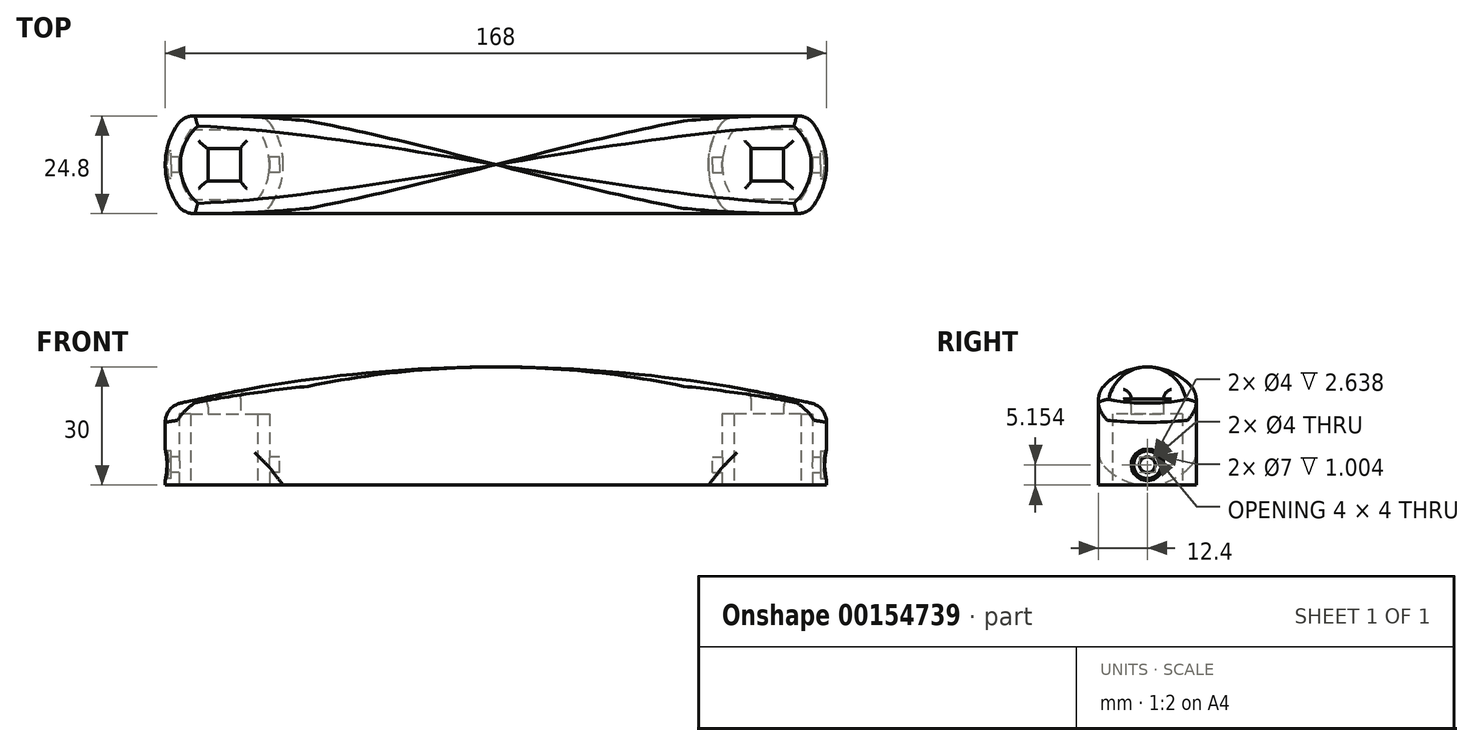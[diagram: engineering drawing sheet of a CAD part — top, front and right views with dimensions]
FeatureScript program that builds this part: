
annotation { "Feature Type Name" : "Feature", "Feature Type Description" : "" }
export const myFeature = defineFeature(function(context is Context, id is Id, definition is map)
    precondition{}
    {
        {
            var Q0;
            Q0=qCreatedBy(makeId("Top.planeOp"),FACE);
            var sketch = newSketch(context, id + "F0", { "sketchPlane" : qUnion([Q0])});
            skLineSegment(sketch, "E0.bottom", {"start": v(-80.5, 8.9) * mm, "end": v(-77.5, 8.9) * mm, "construction": true});
            skLineSegment(sketch, "E0.top", {"start": v(-80.5, -8.9) * mm, "end": v(-77.5, -8.9) * mm, "construction": true});
            skLineSegment(sketch, "E0.left", {"start": v(-80.5, 8.9) * mm, "end": v(-80.5, -8.9) * mm, "construction": true});
            skLineSegment(sketch, "E0.right", {"start": v(-57.5, 8.9) * mm, "end": v(-57.5, -8.9) * mm, "construction": true});
            skArc(sketch, "E1", {"start": v(-77.5, 8.9) * mm, "mid": v(-80.5, 0) * mm, "end": v(-77.5, -8.9) * mm});
            skLineSegment(sketch, "E2", {"start": v(-69, 8.9) * mm, "end": v(-69, -8.9) * mm, "construction": true});
            skArc(sketch, "E3.MirrorCS", {"start": v(-60.5, 8.9) * mm, "mid": v(-57.5, 0) * mm, "end": v(-60.5, -8.9) * mm});
            skLineSegment(sketch, "E4", {"start": v(-80.5, 0) * mm, "end": v(-57.5, 0) * mm, "construction": true});
            skPoint(sketch, "E4.startSnap0", {"position": v(-80.5, 0) * mm});
            skLineSegment(sketch, "E5", {"start": v(-77.5, 8.9) * mm, "end": v(-77.5, -8.9) * mm, "construction": true});
            skLineSegment(sketch, "E6", {"start": v(0, 8.37) * mm, "end": v(0, -11.71) * mm, "construction": true});
            skLineSegment(sketch, "E7", {"start": v(-77.5, 8.9) * mm, "end": v(-60.5, 8.9) * mm});
            skLineSegment(sketch, "E8", {"start": v(-60.5, 8.9) * mm, "end": v(-57.5, 8.9) * mm, "construction": true});
            skLineSegment(sketch, "E9", {"start": v(-60.5, -8.9) * mm, "end": v(-60.5, -8.9) * mm});
            skLineSegment(sketch, "E10", {"start": v(-77.5, -8.9) * mm, "end": v(-60.5, -8.9) * mm});
            skLineSegment(sketch, "E11", {"start": v(-60.5, -8.9) * mm, "end": v(-57.5, -8.9) * mm, "construction": true});
            skSolve(sketch);
        }
        {
            var Q0;
            Q0=qCreatedBy(makeId("Top.planeOp"),FACE);
            var sketch = newSketch(context, id + "F1", { "sketchPlane" : qUnion([Q0])});
            skLineSegment(sketch, "E12.0", {"start": v(-79.12, 12.4) * mm, "end": v(-58.88, 12.4) * mm});
            skArc(sketch, "E12.1", {"start": v(-79.12, 12.4) * mm, "mid": v(-84, 0) * mm, "end": v(-79.12, -12.4) * mm});
            skLineSegment(sketch, "E12.2", {"start": v(-79.12, -12.4) * mm, "end": v(-58.88, -12.4) * mm});
            skArc(sketch, "E12.3", {"start": v(-58.88, 12.4) * mm, "mid": v(-54, 0) * mm, "end": v(-58.88, -12.4) * mm});
            skLineSegment(sketch, "E13", {"start": v(-84, 0) * mm, "end": v(-84, 12.4) * mm, "construction": true});
            skSolve(sketch);
        }
        {
            var Q0;
            Q0=qCreatedBy(makeId("Front.planeOp"),FACE);
            var sketch = newSketch(context, id + "F2", { "sketchPlane" : qUnion([Q0])});
            skLineSegment(sketch, "E14", {"start": v(0, 15) * mm, "end": v(-39.65, 15) * mm, "construction": true});
            skPoint(sketch, "E15.oppositeSnap0", {"position": v(-19.82, 15) * mm});
            skLineSegment(sketch, "E15.bottom", {"start": v(0, 0) * mm, "end": v(-95, 0) * mm});
            skLineSegment(sketch, "E15.top", {"start": v(0, 15) * mm, "end": v(-95, 15) * mm});
            skLineSegment(sketch, "E15.left", {"start": v(0, 0) * mm, "end": v(0, 15) * mm});
            skLineSegment(sketch, "E15.right", {"start": v(-95, 0) * mm, "end": v(-95, 15) * mm});
            skSolve(sketch);
        }
        {
            var Q0;
            Q0=qSketchRegion(id+"F2",true);
            var Q1;
            Q1=sQuery(id+"F2.wireOp",EDGE,"E15.top");
            revolve(context, id + "F3", {"entities" : qUnion([Q0]), "axis" : qUnion([Q1]), "revolveType" : RevolveType.FULL});
        }
        {
            var Q0;
            Q0=qCreatedBy(makeId("Top.planeOp"),FACE);
            var sketch = newSketch(context, id + "F4", { "sketchPlane" : qUnion([Q0])});
            skArc(sketch, "E16", {"start": v(-79.12, 12.4) * mm, "mid": v(-84, 0) * mm, "end": v(-79.12, -12.4) * mm});
            skLineSegment(sketch, "E17", {"start": v(-79.12, 12.4) * mm, "end": v(0, 12.4) * mm});
            skLineSegment(sketch, "E18", {"start": v(0, 12.4) * mm, "end": v(0, 20.08) * mm});
            skLineSegment(sketch, "E19", {"start": v(0, 20.08) * mm, "end": v(-96.67, 20.08) * mm});
            skLineSegment(sketch, "E20", {"start": v(-96.67, 20.08) * mm, "end": v(-96.67, -24.17) * mm});
            skLineSegment(sketch, "E21", {"start": v(-96.67, -24.17) * mm, "end": v(0, -24.17) * mm});
            skLineSegment(sketch, "E22", {"start": v(0, -24.17) * mm, "end": v(0, -12.4) * mm});
            skLineSegment(sketch, "E23", {"start": v(0, -12.4) * mm, "end": v(-79.12, -12.4) * mm});
            skSolve(sketch);
        }
        {
            var Q0;
            Q0=qSketchRegion(id+"F4",true);
            extrude(context, id + "F5", {"entities" : qUnion([Q0]), "operationType" : NewBodyOperationType.REMOVE, "depth" : 50 * mm});
        }
        {
            var Q0;
            Q0=qSketchRegion(id+"F1",true);
            extrude(context, id + "F6", {"entities" : qUnion([Q0]), "operationType" : NewBodyOperationType.ADD, "depth" : 23 * mm});
        }
        {
            var Q0;
            Q0=qSketchRegion(id+"F0",true);
            extrude(context, id + "F7", {"entities" : qUnion([Q0]), "operationType" : NewBodyOperationType.REMOVE, "depth" : 18 * mm});
        }
        {
            var Q0;
            Q0=makeQuery(id+"F7.boolean.opBoolean","COPY",FACE,{"derivedFrom":makeQuery(id+"F7.opExtrude","CAP_FACE",FACE,{"disambiguationData":[OSD([sQuery(id+"F0.wireOp",EDGE,"E1"),sQuery(id+"F0.wireOp",EDGE,"E3.MirrorCS"),sQuery(id+"F0.wireOp",EDGE,"E7"),sQuery(id+"F0.wireOp",EDGE,"E10")])],"isStart":false})});
            var sketch = newSketch(context, id + "F8", { "sketchPlane" : qUnion([Q0])});
            skLineSegment(sketch, "E24.bottom", {"start": v(-73.13, 4.12) * mm, "end": v(-64.87, 4.12) * mm});
            skLineSegment(sketch, "E24.top", {"start": v(-73.13, -4.12) * mm, "end": v(-64.87, -4.12) * mm});
            skLineSegment(sketch, "E24.left", {"start": v(-73.13, 4.12) * mm, "end": v(-73.13, -4.12) * mm});
            skLineSegment(sketch, "E24.right", {"start": v(-64.88, 4.13) * mm, "end": v(-64.88, -4.13) * mm});
            skLineSegment(sketch, "E25", {"start": v(-69, 4.12) * mm, "end": v(-69, -4.12) * mm, "construction": true});
            skLineSegment(sketch, "E26", {"start": v(-73.13, 0) * mm, "end": v(-64.88, 0) * mm, "construction": true});
            skSolve(sketch);
        }
        {
            var Q0;
            Q0=qSketchRegion(id+"F8",true);
            var Q1;
            Q1=makeQuery(id+"F6.opExtrude","CAP_FACE",FACE,{"disambiguationData":[OSD([sQuery(id+"F1.wireOp",EDGE,"E12.0"),sQuery(id+"F1.wireOp",EDGE,"E12.1"),sQuery(id+"F1.wireOp",EDGE,"E12.2"),sQuery(id+"F1.wireOp",EDGE,"E12.3")])],"isStart":false});
            extrude(context, id + "F9", {"entities" : qUnion([Q0]), "operationType" : NewBodyOperationType.REMOVE, "endBound" : BoundingType.THROUGH_ALL, "oppositeDirection" : true, "endBoundEntityFace" : qUnion([Q1]), "depth" : 25 * mm});
        }
        {
            var Q0;
            Q0=qCreatedBy(makeId("Right.planeOp"),FACE);
            cPlane(context, id + "F10", {"entities" : qUnion([Q0]), "cplaneType" : CPlaneType.OFFSET, "offset" : 90 * mm, "oppositeDirection" : true, "width" : 150 * mm, "height" : 150 * mm});
        }
        {
            var Q0;
            Q0=qCreatedBy(id+"F10.planeOp",FACE);
            var sketch = newSketch(context, id + "F11", { "sketchPlane" : qUnion([Q0])});
            skCircle(sketch, "E27", {"center": v(0, 5.15) * mm, "radius": 2 * mm});
            skSolve(sketch);
        }
        {
            var Q0;
            Q0=qSketchRegion(id+"F11",true);
            extrude(context, id + "F12", {"entities" : qUnion([Q0]), "operationType" : NewBodyOperationType.REMOVE, "depth" : 35 * mm});
        }
        {
            var Q0;
            Q0=qCreatedBy(id+"F10.planeOp",FACE);
            var sketch = newSketch(context, id + "F13", { "sketchPlane" : qUnion([Q0])});
            skCircle(sketch, "E28", {"center": v(0, 5.15) * mm, "radius": 3.5 * mm});
            skSolve(sketch);
        }
        {
            var Q0;
            Q0=qSketchRegion(id+"F13",true);
            extrude(context, id + "F14", {"entities" : qUnion([Q0]), "operationType" : NewBodyOperationType.REMOVE, "depth" : 7.5 * mm});
        }
        {
            var Q0;
            Q0=qCreatedBy(makeId("Front.planeOp"),FACE);
            var sketch = newSketch(context, id + "F15", { "sketchPlane" : qUnion([Q0])});
            skLineSegment(sketch, "E29", {"start": v(-64.87, 24) * mm, "end": v(-80.29, 24) * mm, "construction": true});
            skLineSegment(sketch, "E30", {"start": v(-64.87, 18) * mm, "end": v(-80.42, 18) * mm, "construction": true});
            skLineSegment(sketch, "E31", {"start": v(-64.87, 24) * mm, "end": v(-64.87, 18) * mm, "construction": true});
            skSolve(sketch);
        }
        {
            var Q0;
            Q0=qCreatedBy(makeId("Front.planeOp"),FACE);
            var sketch = newSketch(context, id + "F16", { "sketchPlane" : qUnion([Q0])});
            skArc(sketch, "E32", {"start": v(-133.08, 4.01) * mm, "mid": v(-67.8, 23.44) * mm, "end": v(0, 30) * mm});
            skLineSegment(sketch, "E33", {"start": v(0, 30) * mm, "end": v(-86, 30) * mm, "construction": true});
            skLineSegment(sketch, "E34", {"start": v(-86, 30) * mm, "end": v(-86, 0) * mm, "construction": true});
            skLineSegment(sketch, "E35", {"start": v(-133.08, 4.01) * mm, "end": v(-142.12, 0.34) * mm});
            skLineSegment(sketch, "E36", {"start": v(-142.12, 0.34) * mm, "end": v(-142.12, 44.58) * mm});
            skLineSegment(sketch, "E37", {"start": v(-142.12, 44.58) * mm, "end": v(0, 44.58) * mm});
            skLineSegment(sketch, "E38", {"start": v(0, 44.58) * mm, "end": v(0, 30) * mm});
            skPoint(sketch, "E39", {"position": v(-86, 15) * mm});
            skPoint(sketch, "E40", {"position": v(-64.47, 21.36) * mm});
            skPoint(sketch, "E41", {"position": v(-100.39, 15.46) * mm});
            skSolve(sketch);
        }
        {
            var Q0;
            Q0=qSketchRegion(id+"F16",true);
            extrude(context, id + "F17", {"entities" : qUnion([Q0]), "operationType" : NewBodyOperationType.REMOVE, "oppositeDirection" : true, "depth" : 50 * mm, "symmetric" : true});
        }
        {
            var Q0;
            Q0=makeQuery(id+"F5.boolean.opBoolean","INTERSECT",EDGE,{"disambiguationData":[OD(1.0)],"derivedFrom":[makeQuery(id+"F3.opRevolve","SWEPT_FACE",FACE,{"disambiguationData":[OSD([sQuery(id+"F2.wireOp",EDGE,"E15.bottom")])]}),makeQuery(id+"F5.opExtrude","SWEPT_FACE",FACE,{"disambiguationData":[OSD([sQuery(id+"F4.wireOp",EDGE,"E17")])]})]});
            var Q1;
            Q1=makeQuery(id+"F17.boolean.opBoolean","INTERSECT",EDGE,{"disambiguationData":[OD(0.0)],"derivedFrom":[makeQuery(id+"F5.boolean.opBoolean","SPLIT",FACE,{"disambiguationData":[OD(1.0)],"derivedFrom":makeQuery(id+"F3.opRevolve","SWEPT_FACE",FACE,{"disambiguationData":[OSD([sQuery(id+"F2.wireOp",EDGE,"E15.bottom")])]})}),makeQuery(id+"F17.opExtrude","SWEPT_FACE",FACE,{"disambiguationData":[OSD([sQuery(id+"F16.wireOp",EDGE,"E32")])]})]});
            var Q2;
            Q2=makeQuery(id+"F6.boolean.opBoolean","MERGE",EDGE,{"derivedFrom":[makeQuery(id+"F5.boolean.opBoolean","COPY",EDGE,{"derivedFrom":makeQuery(id+"F5.opExtrude","SWEPT_EDGE",EDGE,{"disambiguationData":[OSD([sQuery(id+"F4.wireOp",EDGE,"E16"),sQuery(id+"F4.wireOp",EDGE,"E17")])]})}),makeQuery(id+"F6.opExtrude","SWEPT_EDGE",EDGE,{"disambiguationData":[OSD([sQuery(id+"F1.wireOp",EDGE,"E12.0"),sQuery(id+"F1.wireOp",EDGE,"E12.1")])]})]});
            var Q3;
            Q3=makeQuery(id+"F17.boolean.opBoolean","INTERSECT",EDGE,{"derivedFrom":[makeQuery(id+"F6.boolean.opBoolean","MERGE",FACE,{"derivedFrom":[makeQuery(id+"F5.boolean.opBoolean","COPY",FACE,{"derivedFrom":makeQuery(id+"F5.opExtrude","SWEPT_FACE",FACE,{"disambiguationData":[OSD([sQuery(id+"F4.wireOp",EDGE,"E16")])]})}),makeQuery(id+"F6.opExtrude","SWEPT_FACE",FACE,{"disambiguationData":[OSD([sQuery(id+"F1.wireOp",EDGE,"E12.1")])]})]}),makeQuery(id+"F17.opExtrude","SWEPT_FACE",FACE,{"disambiguationData":[OSD([sQuery(id+"F16.wireOp",EDGE,"E32")])]})]});
            var Q4;
            Q4=makeQuery(id+"F17.boolean.opBoolean","INTERSECT",EDGE,{"disambiguationData":[OD(1.0)],"derivedFrom":[makeQuery(id+"F5.boolean.opBoolean","SPLIT",FACE,{"disambiguationData":[OD(1.0)],"derivedFrom":makeQuery(id+"F3.opRevolve","SWEPT_FACE",FACE,{"disambiguationData":[OSD([sQuery(id+"F2.wireOp",EDGE,"E15.bottom")])]})}),makeQuery(id+"F17.opExtrude","SWEPT_FACE",FACE,{"disambiguationData":[OSD([sQuery(id+"F16.wireOp",EDGE,"E32")])]})]});
            var Q5;
            Q5=makeQuery(id+"F6.opExtrude","SWEPT_EDGE",EDGE,{"disambiguationData":[OSD([sQuery(id+"F1.wireOp",EDGE,"E12.0"),sQuery(id+"F1.wireOp",EDGE,"E12.3")])]});
            var Q6;
            Q6=makeQuery(id+"F5.boolean.opBoolean","INTERSECT",EDGE,{"disambiguationData":[OD(0.0)],"derivedFrom":[makeQuery(id+"F3.opRevolve","SWEPT_FACE",FACE,{"disambiguationData":[OSD([sQuery(id+"F2.wireOp",EDGE,"E15.bottom")])]}),makeQuery(id+"F5.opExtrude","SWEPT_FACE",FACE,{"disambiguationData":[OSD([sQuery(id+"F4.wireOp",EDGE,"E17")])]})]});
            var Q7;
            Q7=makeQuery(id+"F6.boolean.opBoolean","MERGE",EDGE,{"derivedFrom":[makeQuery(id+"F5.boolean.opBoolean","COPY",EDGE,{"derivedFrom":makeQuery(id+"F5.opExtrude","SWEPT_EDGE",EDGE,{"disambiguationData":[OSD([sQuery(id+"F4.wireOp",EDGE,"E16"),sQuery(id+"F4.wireOp",EDGE,"E23")])]})}),makeQuery(id+"F6.opExtrude","SWEPT_EDGE",EDGE,{"disambiguationData":[OSD([sQuery(id+"F1.wireOp",EDGE,"E12.1"),sQuery(id+"F1.wireOp",EDGE,"E12.2")])]})]});
            var Q8;
            Q8=makeQuery(id+"F5.boolean.opBoolean","INTERSECT",EDGE,{"disambiguationData":[OD(1.0)],"derivedFrom":[makeQuery(id+"F3.opRevolve","SWEPT_FACE",FACE,{"disambiguationData":[OSD([sQuery(id+"F2.wireOp",EDGE,"E15.bottom")])]}),makeQuery(id+"F5.opExtrude","SWEPT_FACE",FACE,{"disambiguationData":[OSD([sQuery(id+"F4.wireOp",EDGE,"E23")])]})]});
            var Q9;
            Q9=makeQuery(id+"F6.opExtrude","SWEPT_EDGE",EDGE,{"disambiguationData":[OSD([sQuery(id+"F1.wireOp",EDGE,"E12.2"),sQuery(id+"F1.wireOp",EDGE,"E12.3")])]});
            var Q10;
            Q10=makeQuery(id+"F5.boolean.opBoolean","INTERSECT",EDGE,{"disambiguationData":[OD(0.0)],"derivedFrom":[makeQuery(id+"F3.opRevolve","SWEPT_FACE",FACE,{"disambiguationData":[OSD([sQuery(id+"F2.wireOp",EDGE,"E15.bottom")])]}),makeQuery(id+"F5.opExtrude","SWEPT_FACE",FACE,{"disambiguationData":[OSD([sQuery(id+"F4.wireOp",EDGE,"E23")])]})]});
            fillet(context, id + "F18", {"entities" : qUnion([Q0, Q1, Q2, Q3, Q4, Q5, Q6, Q7, Q8, Q9, Q10]), "radius" : 5 * mm, "tangentPropagation" : true, "allowEdgeOverflow" : false});
        }
        {
            var Q0;
            Q0=makeQuery(id+"F17.boolean.opBoolean","INTERSECT",EDGE,{"derivedFrom":[makeQuery(id+"F9.boolean.opBoolean","COPY",FACE,{"derivedFrom":makeQuery(id+"F9.opExtrude","SWEPT_FACE",FACE,{"disambiguationData":[OSD([sQuery(id+"F8.wireOp",EDGE,"E24.top")])]})}),makeQuery(id+"F17.opExtrude","SWEPT_FACE",FACE,{"disambiguationData":[OSD([sQuery(id+"F16.wireOp",EDGE,"E32")])]})]});
            var Q1;
            Q1=makeQuery(id+"F17.boolean.opBoolean","INTERSECT",EDGE,{"derivedFrom":[makeQuery(id+"F9.boolean.opBoolean","COPY",FACE,{"derivedFrom":makeQuery(id+"F9.opExtrude","SWEPT_FACE",FACE,{"disambiguationData":[OSD([sQuery(id+"F8.wireOp",EDGE,"E24.right")])]})}),makeQuery(id+"F17.opExtrude","SWEPT_FACE",FACE,{"disambiguationData":[OSD([sQuery(id+"F16.wireOp",EDGE,"E32")])]})]});
            var Q2;
            Q2=makeQuery(id+"F17.boolean.opBoolean","INTERSECT",EDGE,{"derivedFrom":[makeQuery(id+"F9.boolean.opBoolean","COPY",FACE,{"derivedFrom":makeQuery(id+"F9.opExtrude","SWEPT_FACE",FACE,{"disambiguationData":[OSD([sQuery(id+"F8.wireOp",EDGE,"E24.left")])]})}),makeQuery(id+"F17.opExtrude","SWEPT_FACE",FACE,{"disambiguationData":[OSD([sQuery(id+"F16.wireOp",EDGE,"E32")])]})]});
            var Q3;
            Q3=makeQuery(id+"F17.boolean.opBoolean","INTERSECT",EDGE,{"derivedFrom":[makeQuery(id+"F9.boolean.opBoolean","COPY",FACE,{"derivedFrom":makeQuery(id+"F9.opExtrude","SWEPT_FACE",FACE,{"disambiguationData":[OSD([sQuery(id+"F8.wireOp",EDGE,"E24.bottom")])]})}),makeQuery(id+"F17.opExtrude","SWEPT_FACE",FACE,{"disambiguationData":[OSD([sQuery(id+"F16.wireOp",EDGE,"E32")])]})]});
            fillet(context, id + "F19", {"entities" : qUnion([Q0, Q1, Q2, Q3]), "radius" : 2 * mm, "tangentPropagation" : true, "allowEdgeOverflow" : false});
        }
        {
            var Q0;
            Q0=makeQuery(id+"F14.boolean.opBoolean","INTERSECT",EDGE,{"derivedFrom":[makeQuery(id+"F6.boolean.opBoolean","MERGE",FACE,{"derivedFrom":[makeQuery(id+"F5.boolean.opBoolean","COPY",FACE,{"derivedFrom":makeQuery(id+"F5.opExtrude","SWEPT_FACE",FACE,{"disambiguationData":[OSD([sQuery(id+"F4.wireOp",EDGE,"E16")])]})}),makeQuery(id+"F6.opExtrude","SWEPT_FACE",FACE,{"disambiguationData":[OSD([sQuery(id+"F1.wireOp",EDGE,"E12.1")])]})]}),makeQuery(id+"F14.opExtrude","SWEPT_FACE",FACE,{"disambiguationData":[OSD([sQuery(id+"F13.wireOp",EDGE,"E28")])]})]});
            fillet(context, id + "F20", {"entities" : qUnion([Q0]), "radius" : 0.5 * mm, "tangentPropagation" : true, "allowEdgeOverflow" : false});
        }
        {
            var Q0;
            Q0=makeQuery(id+"F3.opRevolve","SWEPT_BODY",BODY,{"disambiguationData":[OSD([sQuery(id+"F2.wireOp",EDGE,"E15.bottom"),sQuery(id+"F2.wireOp",EDGE,"E15.top"),sQuery(id+"F2.wireOp",EDGE,"E15.left"),sQuery(id+"F2.wireOp",EDGE,"E15.right")])]});
            var Q1;
            Q1=makeQuery(id+"F3.opRevolve","SWEPT_FACE",FACE,{"disambiguationData":[OSD([sQuery(id+"F2.wireOp",EDGE,"E15.left")])]});
            mirror(context, id + "F21", {"operationType" : NewBodyOperationType.ADD, "entities" : qUnion([Q0]), "mirrorPlane" : qUnion([Q1])});
        }
    });
